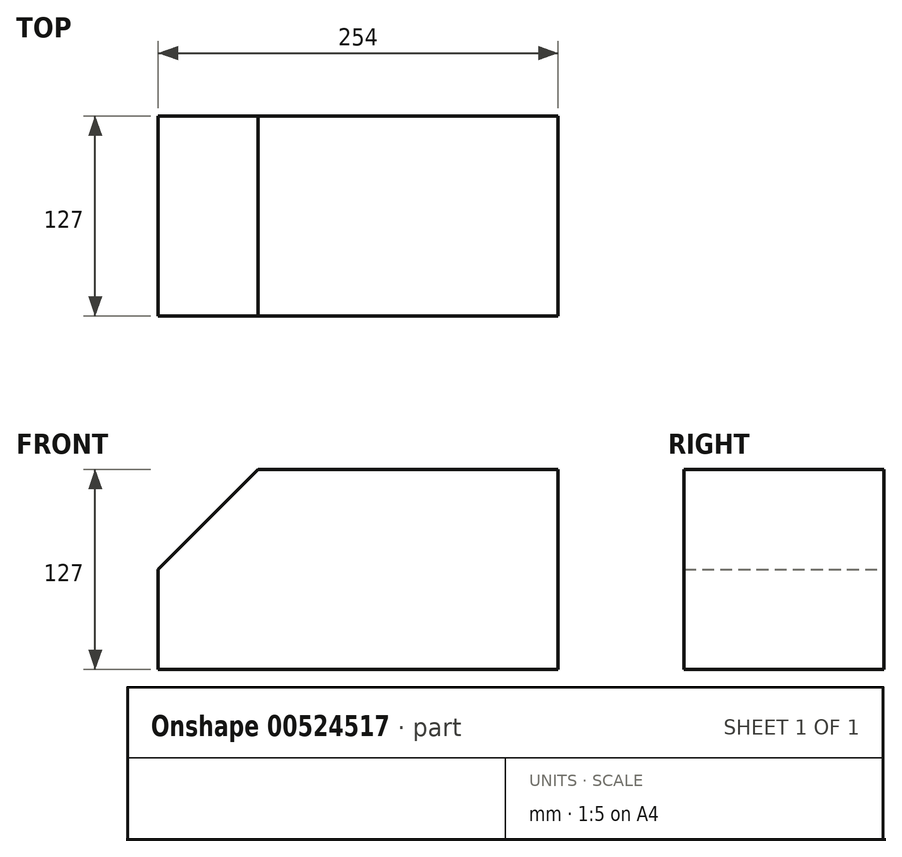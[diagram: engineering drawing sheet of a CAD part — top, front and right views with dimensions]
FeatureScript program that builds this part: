
annotation { "Feature Type Name" : "Feature", "Feature Type Description" : "" }
export const myFeature = defineFeature(function(context is Context, id is Id, definition is map)
    precondition{}
    {
        {
            var Q0;
            Q0=qCreatedBy(makeId("Front.planeOp"),FACE);
            var sketch = newSketch(context, id + "F0", { "sketchPlane" : qUnion([Q0])});
            skLineSegment(sketch, "E0", {"start": v(0, 0) * mm, "end": v(254, 0) * mm});
            skLineSegment(sketch, "E1", {"start": v(254, 0) * mm, "end": v(254, 127) * mm});
            skLineSegment(sketch, "E2", {"start": v(254, 127) * mm, "end": v(63.5, 127) * mm});
            skLineSegment(sketch, "E3", {"start": v(63.5, 127) * mm, "end": v(0, 63.5) * mm});
            skLineSegment(sketch, "E4", {"start": v(0, 63.5) * mm, "end": v(0, 0) * mm});
            skSolve(sketch);
        }
        {
            var Q0;
            Q0 = qSketchRegion(id + "F0", true);
            extrude(context, id + "F1", {"entities" : qUnion([Q0]), "depth" : 127 * mm, "offsetDistance" : 25.4 * mm});
        }
    });
